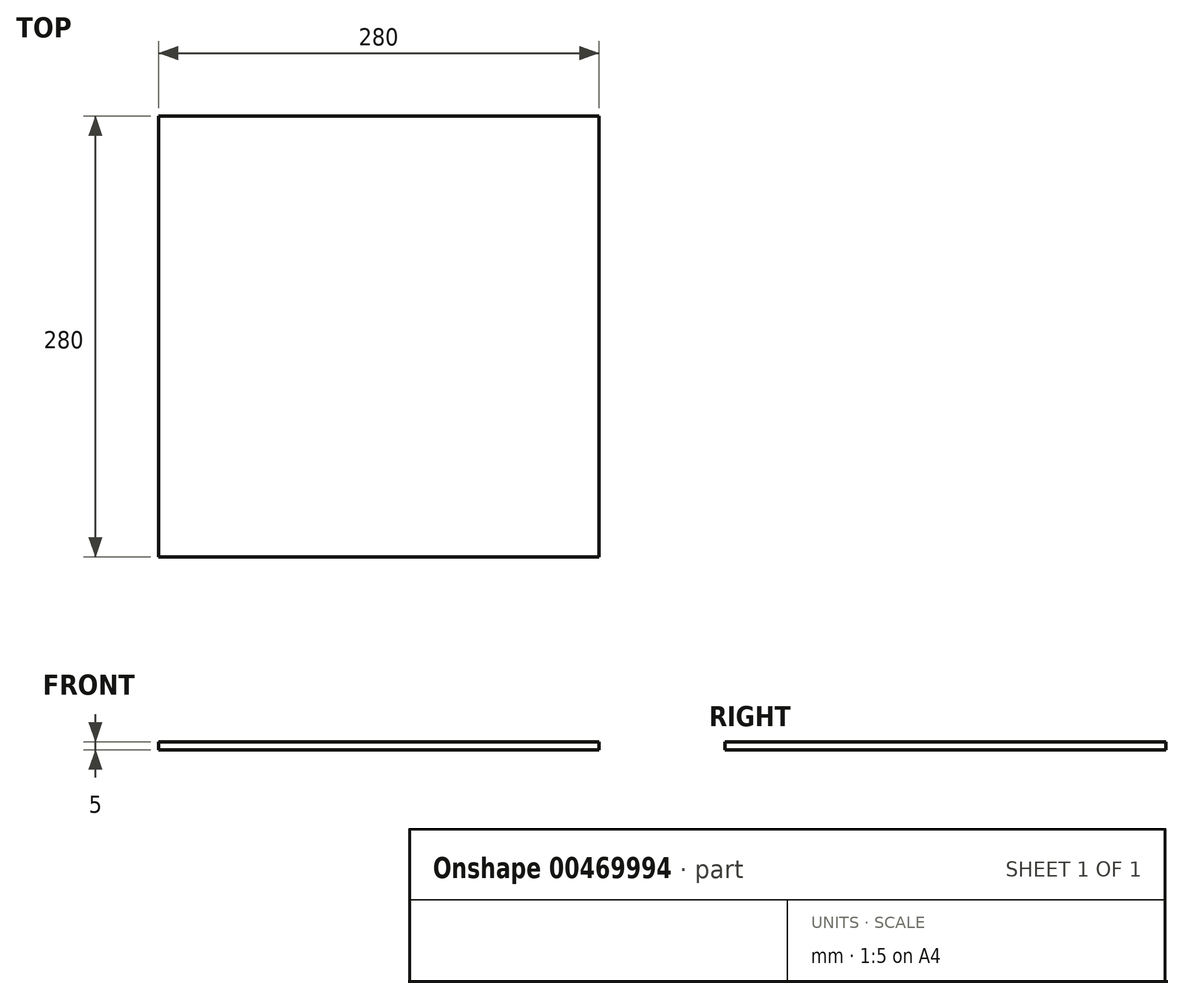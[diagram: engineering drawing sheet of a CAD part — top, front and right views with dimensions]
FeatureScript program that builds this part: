
annotation { "Feature Type Name" : "Feature", "Feature Type Description" : "" }
export const myFeature = defineFeature(function(context is Context, id is Id, definition is map)
    precondition{}
    {
        {
            var Q0;
            Q0=qCreatedBy(makeId("Top.planeOp"),FACE);
            var sketch = newSketch(context, id + "F0", { "sketchPlane" : qUnion([Q0])});
            skLineSegment(sketch, "E0.bottom", {"start": v(140, -140) * mm, "end": v(-140, -140) * mm});
            skLineSegment(sketch, "E0.top", {"start": v(140, 140) * mm, "end": v(-140, 140) * mm});
            skLineSegment(sketch, "E0.left", {"start": v(140, -140) * mm, "end": v(140, 140) * mm});
            skLineSegment(sketch, "E0.right", {"start": v(-140, -140) * mm, "end": v(-140, 140) * mm});
            skPoint(sketch, "E0.middle", {"position": v(0, 0) * mm});
            skSolve(sketch);
        }
        {
            var Q0;
            Q0 = qSketchRegion(id + "F0", true);
            extrude(context, id + "F1", {"entities" : qUnion([Q0]), "depth" : 5 * mm});
        }
    });
